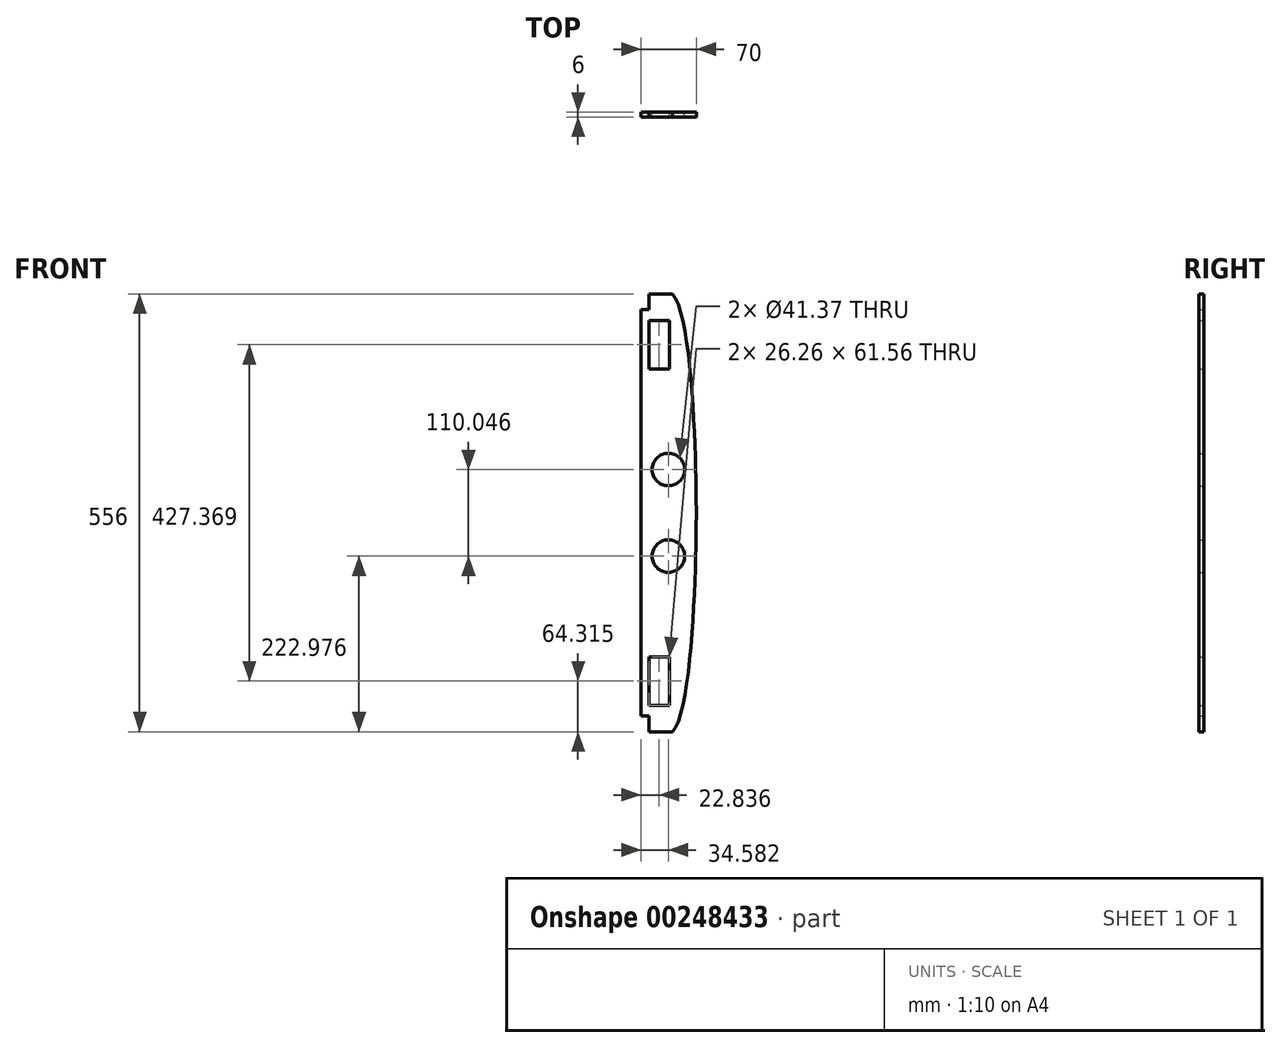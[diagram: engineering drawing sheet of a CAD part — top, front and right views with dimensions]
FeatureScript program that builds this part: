
annotation { "Feature Type Name" : "Feature", "Feature Type Description" : "" }
export const myFeature = defineFeature(function(context is Context, id is Id, definition is map)
    precondition{}
    {
        {
            var Q0;
            Q0=qCreatedBy(makeId("Front.planeOp"),FACE);
            var sketch = newSketch(context, id + "F0", { "sketchPlane" : qUnion([Q0])});
            skLineSegment(sketch, "E0.bottom", {"start": v(-25.34, -282.3) * mm, "end": v(-85.34, -282.3) * mm});
            skLineSegment(sketch, "E0.top", {"start": v(-25.34, 273.7) * mm, "end": v(-85.34, 273.7) * mm});
            skLineSegment(sketch, "E0.left", {"start": v(-25.34, -282.3) * mm, "end": v(-25.34, 273.7) * mm});
            skLineSegment(sketch, "E1", {"start": v(-25.34, -282.3) * mm, "end": v(-25.34, -4.3) * mm});
            skLineSegment(sketch, "E2", {"start": v(-95.34, -4.3) * mm, "end": v(-52.18, -4.3) * mm});
            skLineSegment(sketch, "E3", {"start": v(-52.18, -4.3) * mm, "end": v(-25.34, -4.3) * mm});
            skFitSpline(sketch, "E4", {"points": [v(-55.34, 273.7) * mm, v(-25.34, -4.3) * mm], "startDerivative": vector(90, -101.37) * mm, "endDerivative": vector(0, -12.9) * mm});
            skFitSpline(sketch, "E5.MirrorCS", {"points": [v(-55.34, -282.3) * mm, v(-25.34, -4.3) * mm], "startDerivative": vector(90, 101.37) * mm, "endDerivative": vector(0, 12.9) * mm});
            skPoint(sketch, "E6.visualSharp", {"position": v(-55.34, 256.55) * mm});
            skPoint(sketch, "E7.MirrorP", {"position": v(-55.34, -265.15) * mm});
            skCircle(sketch, "E8", {"center": v(-60.76, 50.72) * mm, "radius": 20.68 * mm});
            skCircle(sketch, "E9.MirrorC", {"center": v(-60.76, -59.32) * mm, "radius": 20.68 * mm});
            skLineSegment(sketch, "E10", {"start": v(-25.34, -4.3) * mm, "end": v(-95.34, -4.3) * mm});
            skLineSegment(sketch, "E11", {"start": v(-60.34, -4.3) * mm, "end": v(-60.34, -9.3) * mm});
            skLineSegment(sketch, "E12", {"start": v(-60.34, -4.3) * mm, "end": v(-60.34, 0.7) * mm});
            skLineSegment(sketch, "E13", {"start": v(-60.34, 0.7) * mm, "end": v(-95.34, 0.7) * mm});
            skLineSegment(sketch, "E14", {"start": v(-60.34, -9.3) * mm, "end": v(-95.34, -9.3) * mm});
            skLineSegment(sketch, "E15", {"start": v(-85.34, 273.7) * mm, "end": v(-85.34, 253.7) * mm});
            skLineSegment(sketch, "E16", {"start": v(-85.34, 253.7) * mm, "end": v(-95.34, 253.7) * mm});
            skLineSegment(sketch, "E17", {"start": v(-85.34, 273.7) * mm, "end": v(-55.34, 273.7) * mm});
            skLineSegment(sketch, "E18.MirrorCS", {"start": v(-85.34, -282.3) * mm, "end": v(-85.34, -262.3) * mm});
            skLineSegment(sketch, "E19.MirrorCS", {"start": v(-85.34, -262.3) * mm, "end": v(-95.34, -262.3) * mm});
            skLineSegment(sketch, "E20", {"start": v(-95.34, -262.3) * mm, "end": v(-95.34, 253.7) * mm});
            skLineSegment(sketch, "E21.bottom", {"start": v(-59.37, 240.16) * mm, "end": v(-85.64, 240.16) * mm});
            skLineSegment(sketch, "E21.top", {"start": v(-59.37, 178.6) * mm, "end": v(-85.64, 178.6) * mm});
            skLineSegment(sketch, "E21.left", {"start": v(-59.37, 240.16) * mm, "end": v(-59.37, 178.6) * mm});
            skLineSegment(sketch, "E21.right", {"start": v(-85.64, 240.16) * mm, "end": v(-85.64, 178.6) * mm});
            skLineSegment(sketch, "E22.MirrorCS", {"start": v(-59.37, -248.76) * mm, "end": v(-85.64, -248.76) * mm});
            skLineSegment(sketch, "E23.MirrorCS", {"start": v(-59.37, -248.76) * mm, "end": v(-59.37, -187.2) * mm});
            skLineSegment(sketch, "E24.MirrorCS", {"start": v(-85.64, -248.76) * mm, "end": v(-85.64, -187.2) * mm});
            skLineSegment(sketch, "E25.MirrorCS", {"start": v(-59.37, -187.2) * mm, "end": v(-85.64, -187.2) * mm});
            skSolve(sketch);
        }
        {
            var Q0;
            Q0=makeQuery(id+"F0.imprint","IMPRINT",FACE,{"disambiguationData":[TD([[makeQuery(id+"F0.imprint","IMPRINT",EDGE,{"derivedFrom":sQuery(id+"F0.wireOp",EDGE,"wO8yRAjj-VujT-FsJF-D8KV-fRzdfIzrzO8W")}),-1.0]])]});
            var Q1;
            Q1=makeQuery(id+"F0.imprint","IMPRINT",FACE,{"disambiguationData":[TD([[makeQuery(id+"F0.imprint","IMPRINT",EDGE,{"derivedFrom":sQuery(id+"F0.wireOp",EDGE,"fdfiE9YE-azMK-5wJ3-DYWj-UjI7CARbdNxR")}),1.0]])]});
            var Q2;
            {var subQ2=sQuery(id+"F0.wireOp",EDGE,"E2");Q2=makeQuery(id+"F0.imprint","IMPRINT",FACE,{"disambiguationData":[TD([[makeQuery(id+"F0.imprint","IMPRINT",EDGE,{"derivedFrom":subQ2}),1.0]])]});}
            var Q3;
            {var subQ4=sQuery(id+"F0.wireOp",EDGE,"E2");Q3=makeQuery(id+"F0.imprint","IMPRINT",FACE,{"disambiguationData":[TD([[makeQuery(id+"F0.imprint","IMPRINT",EDGE,{"derivedFrom":subQ4}),-1.0]])]});}
            var Q4;
            {var subQ3=sQuery(id+"F0.wireOp",EDGE,"4MwfRvzT-bVmI-76KQ-HtM8-0Gz24QdNIZgF");Q4=makeQuery(id+"F0.imprint","IMPRINT",FACE,{"disambiguationData":[TD([[makeQuery(id+"F0.imprint","IMPRINT",EDGE,{"derivedFrom":subQ3}),-1.0]])]});}
            var Q5;
            {var subQ0=sQuery(id+"F0.wireOp",EDGE,"E5.MirrorCS");Q5=makeQuery(id+"F0.imprint","IMPRINT",FACE,{"disambiguationData":[TD([[makeQuery(id+"F0.imprint","IMPRINT",EDGE,{"derivedFrom":subQ0}),1.0]])]});}
            var Q6;
            {var subQ4=sQuery(id+"F0.wireOp",EDGE,"E4");Q6=makeQuery(id+"F0.imprint","IMPRINT",FACE,{"disambiguationData":[TD([[makeQuery(id+"F0.imprint","IMPRINT",EDGE,{"derivedFrom":subQ4}),-1.0]])]});}
            extrude(context, id + "F1", {"entities" : qUnion([Q0, Q1, Q2, Q3, Q4, Q5, Q6]), "depth" : 6 * mm});
        }
    });
